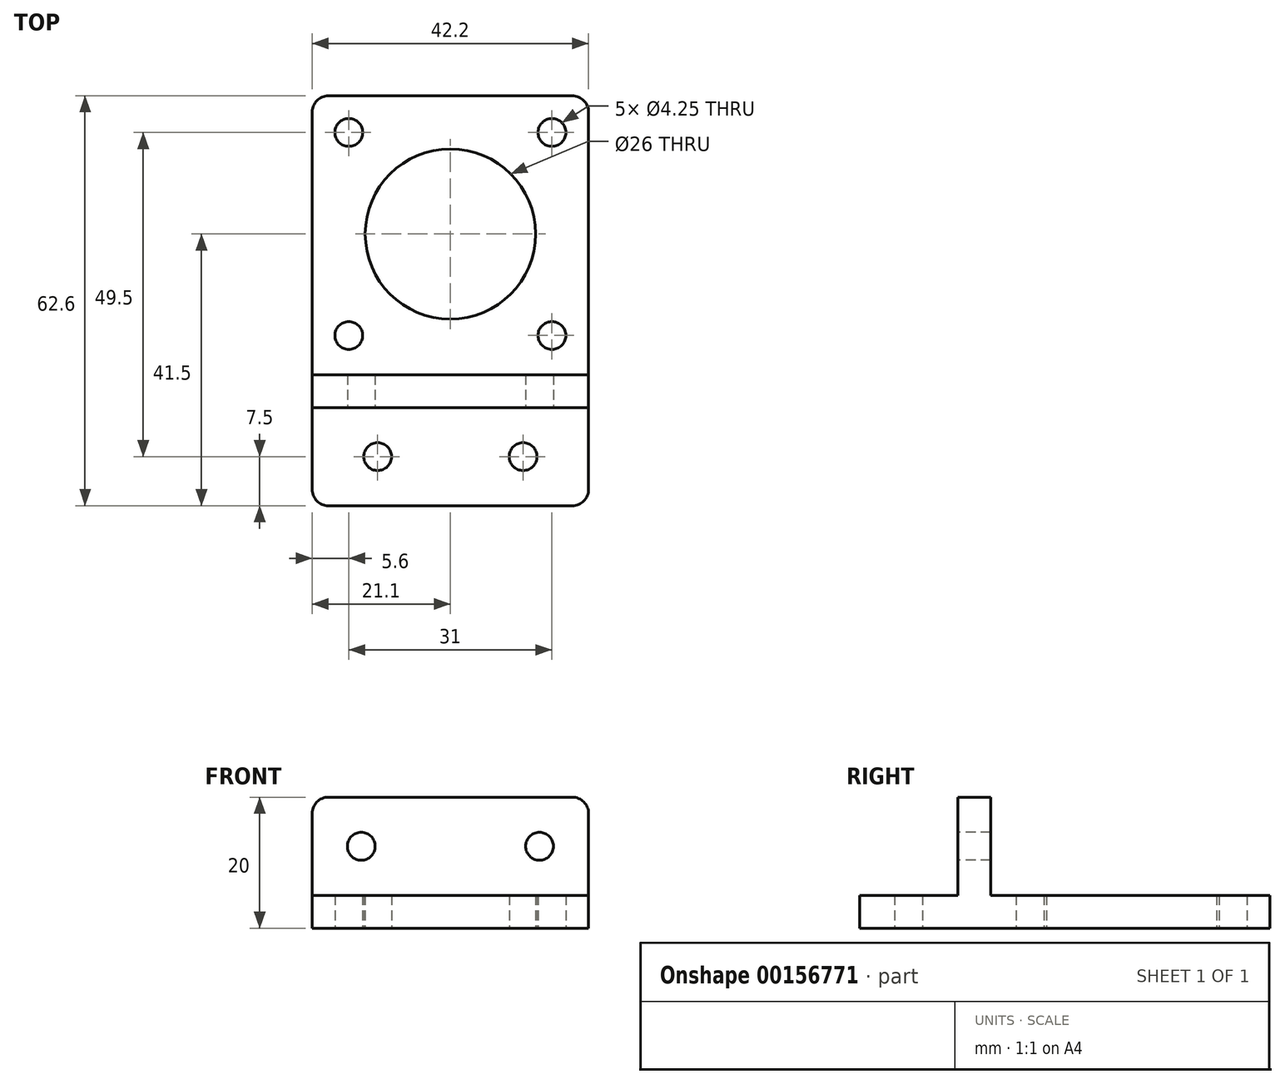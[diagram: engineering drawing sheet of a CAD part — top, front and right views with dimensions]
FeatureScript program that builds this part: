
annotation { "Feature Type Name" : "Feature", "Feature Type Description" : "" }
export const myFeature = defineFeature(function(context is Context, id is Id, definition is map)
    precondition{}
    {
        {
            var Q0;
            Q0=qCreatedBy(makeId("Top.planeOp"),FACE);
            var sketch = newSketch(context, id + "F0", { "sketchPlane" : qUnion([Q0])});
            skLineSegment(sketch, "E0.bottom", {"start": v(15.5, -15.5) * mm, "end": v(-15.5, -15.5) * mm, "construction": true});
            skLineSegment(sketch, "E0.top", {"start": v(15.5, 15.5) * mm, "end": v(-15.5, 15.5) * mm, "construction": true});
            skLineSegment(sketch, "E0.left", {"start": v(15.5, -15.5) * mm, "end": v(15.5, 15.5) * mm, "construction": true});
            skLineSegment(sketch, "E0.right", {"start": v(-15.5, -15.5) * mm, "end": v(-15.5, 15.5) * mm, "construction": true});
            skPoint(sketch, "E0.middle", {"position": v(0, 0) * mm});
            skCircle(sketch, "E1", {"center": v(-15.5, 15.5) * mm, "radius": 2.12 * mm});
            skCircle(sketch, "E2", {"center": v(-15.5, -15.5) * mm, "radius": 2.12 * mm});
            skCircle(sketch, "E3", {"center": v(15.5, -15.5) * mm, "radius": 2.12 * mm});
            skCircle(sketch, "E4", {"center": v(15.5, 15.5) * mm, "radius": 2.12 * mm});
            skCircle(sketch, "E5", {"center": v(0, 0) * mm, "radius": 13 * mm});
            skLineSegment(sketch, "E6", {"start": v(0, 21.1) * mm, "end": v(-18.6, 21.1) * mm});
            skLineSegment(sketch, "E7", {"start": v(-21.1, 18.6) * mm, "end": v(-21.1, -39) * mm});
            skLineSegment(sketch, "E8", {"start": v(-18.6, -41.5) * mm, "end": v(0, -41.5) * mm});
            skCircle(sketch, "E9", {"center": v(-11.1, -34) * mm, "radius": 2.12 * mm});
            skLineSegment(sketch, "E10.MirrorCS", {"start": v(0, 21.1) * mm, "end": v(18.6, 21.1) * mm});
            skLineSegment(sketch, "E11.MirrorCS", {"start": v(21.1, 18.6) * mm, "end": v(21.1, -39) * mm});
            skLineSegment(sketch, "E12.MirrorCS", {"start": v(18.6, -41.5) * mm, "end": v(0, -41.5) * mm});
            skCircle(sketch, "E13.MirrorC", {"center": v(11.1, -34) * mm, "radius": 2.12 * mm});
            skPoint(sketch, "E14.visualSharp", {"position": v(-21.1, 21.1) * mm});
            skArc(sketch, "E14.filletArc", {"start": v(-18.6, 21.1) * mm, "mid": v(-20.37, 20.37) * mm, "end": v(-21.1, 18.6) * mm});
            skPoint(sketch, "E15.visualSharp", {"position": v(21.1, -41.5) * mm});
            skArc(sketch, "E15.filletArc", {"start": v(18.6, -41.5) * mm, "mid": v(20.37, -40.77) * mm, "end": v(21.1, -39) * mm});
            skPoint(sketch, "E16.visualSharp", {"position": v(-21.1, -41.5) * mm});
            skArc(sketch, "E16.filletArc", {"start": v(-21.1, -39) * mm, "mid": v(-20.37, -40.77) * mm, "end": v(-18.6, -41.5) * mm});
            skPoint(sketch, "E17.visualSharp", {"position": v(21.1, 21.1) * mm});
            skArc(sketch, "E17.filletArc", {"start": v(21.1, 18.6) * mm, "mid": v(20.37, 20.37) * mm, "end": v(18.6, 21.1) * mm});
            skSolve(sketch);
        }
        {
            var Q0;
            Q0=qSketchRegion(id+"F0",true);
            extrude(context, id + "F1", {"entities" : qUnion([Q0]), "depth" : 5 * mm});
        }
        {
            var Q0;
            Q0=makeQuery(id+"F1.opExtrude","CAP_FACE",FACE,{"disambiguationData":[OSD([sQuery(id+"F0.wireOp",EDGE,"E1"),sQuery(id+"F0.wireOp",EDGE,"E2"),sQuery(id+"F0.wireOp",EDGE,"E3"),sQuery(id+"F0.wireOp",EDGE,"E4"),sQuery(id+"F0.wireOp",EDGE,"E5"),sQuery(id+"F0.wireOp",EDGE,"E6"),sQuery(id+"F0.wireOp",EDGE,"E7"),sQuery(id+"F0.wireOp",EDGE,"E8"),sQuery(id+"F0.wireOp",EDGE,"E9"),sQuery(id+"F0.wireOp",EDGE,"E10.MirrorCS"),sQuery(id+"F0.wireOp",EDGE,"E11.MirrorCS"),sQuery(id+"F0.wireOp",EDGE,"E12.MirrorCS"),sQuery(id+"F0.wireOp",EDGE,"E13.MirrorC")])],"isStart":false});
            var sketch = newSketch(context, id + "F2", { "sketchPlane" : qUnion([Q0])});
            skLineSegment(sketch, "E18.bottom", {"start": v(21.1, -26.5) * mm, "end": v(-21.1, -26.5) * mm});
            skLineSegment(sketch, "E18.top", {"start": v(21.1, -21.5) * mm, "end": v(-21.1, -21.5) * mm});
            skLineSegment(sketch, "E18.left", {"start": v(21.1, -26.5) * mm, "end": v(21.1, -21.5) * mm});
            skLineSegment(sketch, "E18.right", {"start": v(-21.1, -26.5) * mm, "end": v(-21.1, -21.5) * mm});
            skPoint(sketch, "E18.middle", {"position": v(0, -24) * mm});
            skSolve(sketch);
        }
        {
            var Q0;
            Q0=qSketchRegion(id+"F2",true);
            extrude(context, id + "F3", {"entities" : qUnion([Q0]), "operationType" : NewBodyOperationType.ADD, "depth" : 15 * mm});
        }
        {
            var Q0;
            Q0=makeQuery(id+"F3.opExtrude","SWEPT_FACE",FACE,{"disambiguationData":[OSD([sQuery(id+"F2.wireOp",EDGE,"E18.bottom")])]});
            var sketch = newSketch(context, id + "F4", { "sketchPlane" : qUnion([Q0])});
            skCircle(sketch, "E19", {"center": v(-13.6, 12.5) * mm, "radius": 2.12 * mm});
            skCircle(sketch, "E20", {"center": v(13.6, 12.5) * mm, "radius": 2.12 * mm});
            skSolve(sketch);
        }
        {
            var Q0;
            Q0=qSketchRegion(id+"F4",true);
            extrude(context, id + "F5", {"entities" : qUnion([Q0]), "operationType" : NewBodyOperationType.REMOVE, "endBound" : BoundingType.THROUGH_ALL, "oppositeDirection" : true, "depth" : 25 * mm});
        }
        {
            var Q0;
            Q0=makeQuery(id+"F3.opExtrude","CAP_EDGE",EDGE,{"disambiguationData":[OSD([sQuery(id+"F2.wireOp",EDGE,"E18.right")])],"isStart":false});
            var Q1;
            Q1=makeQuery(id+"F3.opExtrude","CAP_EDGE",EDGE,{"disambiguationData":[OSD([sQuery(id+"F2.wireOp",EDGE,"E18.left")])],"isStart":false});
            fillet(context, id + "F6", {"entities" : qUnion([Q0, Q1]), "radius" : 2.5 * mm, "tangentPropagation" : true, "allowEdgeOverflow" : false});
        }
    });
